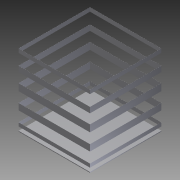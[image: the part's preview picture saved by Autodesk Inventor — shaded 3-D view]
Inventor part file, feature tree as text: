
AUTODESK INVENTOR PART (.ipt)
format: ipt  version: 2011 SP2 (Build 150309200, 309)  size: 133,120 bytes
history: native  units: mm
features: extrude x3, sketch x3
ambient origin geometry x8: Origin, YZ Plane, XZ Plane, XY Plane, X Axis, Y Axis, Z Axis, Center Point
bodies: Solid1 (feature_tree)
feature tree (6):
  extrude  "Extrusion1"  Depth=200.0mm
  extrude  "Extrusion2"  Depth=0.2mm
  extrude  "Extrusion3"  Depth=0.2mm
  sketch  "Sketch1"  dims[d0=200.0mm d1=200.0mm]
  sketch  "Sketch2"  dims[d2=2.0mm d3=0.0mm d4=0.2mm]
  sketch  "Sketch3"  dims[d5=0.2mm d6=0.2mm d7=0.2mm d8=200.0mm d9=2.0mm d10=0.0mm d11=0.0mm d12=200.0mm d13=0.0mm]
